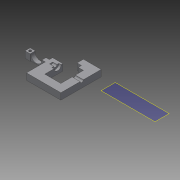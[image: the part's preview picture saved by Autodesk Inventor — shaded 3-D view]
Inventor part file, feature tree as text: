
AUTODESK INVENTOR PART (.ipt)
format: ipt  version: 2016 (Build 200138000, 138)  size: 287,744 bytes
history: native  units: mm
features: extrude x10, sketch x10, chamfer x8, reference x8, plane x1
ambient origin geometry x8: Origin, YZ Plane, XZ Plane, XY Plane, X Axis, Y Axis, Z Axis, Center Point
bodies: Solid1 (feature_tree)
feature tree (37):
  plane  "Work Plane1"
  extrude  "Extrusion1"  Depth=12.7mm
  extrude  "Extrusion2"  Depth=20.0mm
  extrude  "Extrusion3"  Depth=10.0mm
  extrude  "Extrusion4"  Depth=25.0mm
  extrude  "Extrusion5"  Depth=20.0mm
  extrude  "Extrusion6"  Depth=15.0mm
  extrude  "Extrusion7"  Depth=25.0mm
  extrude  "Extrusion8"  Depth=20.0mm
  extrude  "Extrusion9"  Depth=16.0mm
  extrude  "Extrusion10"  Depth=10.0mm TaperAngle=0.0deg
  chamfer  "Chamfer1"  Distance=8.0mm
  chamfer  "Chamfer2"  Distance=10.0mm
  chamfer  "Chamfer3"  Distance=10.0mm
  chamfer  "Chamfer4"  Distance=95.0mm
  chamfer  "Chamfer5"  Distance=22.0mm
  chamfer  "Chamfer6"  Distance=7.0mm
  chamfer  "Chamfer7"  Distance=22.0mm
  chamfer  "Chamfer8"  Distance=15.0mm
  sketch  "Sketch1"  dims[d0=12.7mm d1=2.0mm]
  reference  "Reference1"
  reference  "Reference2"
  reference  "Reference3"
  reference  "Reference4"
  sketch  "Sketch2"  dims[d2=1.0mm d3=20.0mm]
  reference  "Reference5"
  sketch  "Sketch3"  dims[d4=16.0mm d5=10.0mm]
  sketch  "Sketch4"  dims[d6=40.0mm d7=25.0mm]
  sketch  "Sketch5"  dims[d8=50.0mm d9=20.0mm]
  reference  "Reference6"
  sketch  "Sketch6"  dims[d10=20.0mm d11=15.0mm]
  sketch  "Sketch7"  dims[d12=14.0mm d13=25.0mm]
  sketch  "Sketch8"  dims[d14=20.0mm d15=0.0mm d16=34.925mm]
  sketch  "Sketch9"  dims[d17=20.0mm d18=0.0mm d19=16.0mm]
  reference  "Reference7"
  reference  "Reference8"
  sketch  "Sketch10"  dims[d20=16.0mm d21=10.0mm d22=0.0mm d23=8.0mm d24=10.0mm d25=0.0mm d26=10.0mm d27=95.0mm d28=0.0mm d29=22.0mm d30=7.0mm d31=0.0mm d32=22.0mm d33=15.0mm d34=0.0mm d35=16.0mm d36=16.0mm d37=15.0mm d38=0.0mm d39=8.0mm d40=15.0mm d41=0.0mm d42=8.0mm d43=8.0mm d46=8.0mm d47=25.0mm d48=8.0mm d49=8.0mm d50=12.0mm d51=15.0mm d52=15.0mm d53=8.0mm d54=40.0mm d55=10.0mm d56=15.0mm d57=0.0mm d58=5.0mm d59=2.0mm d60=45.0deg d61=10.0mm d62=2.0mm d63=45.0deg d64=5.0mm d65=2.0mm d66=45.0deg d67=5.0mm d68=2.0mm d69=45.0deg d70=10.0mm d71=2.0mm d72=45.0deg d73=10.0mm d74=2.0mm d75=45.0deg d76=10.0mm d77=2.0mm d78=45.0deg d79=5.0mm d80=2.0mm d81=45.0deg]
